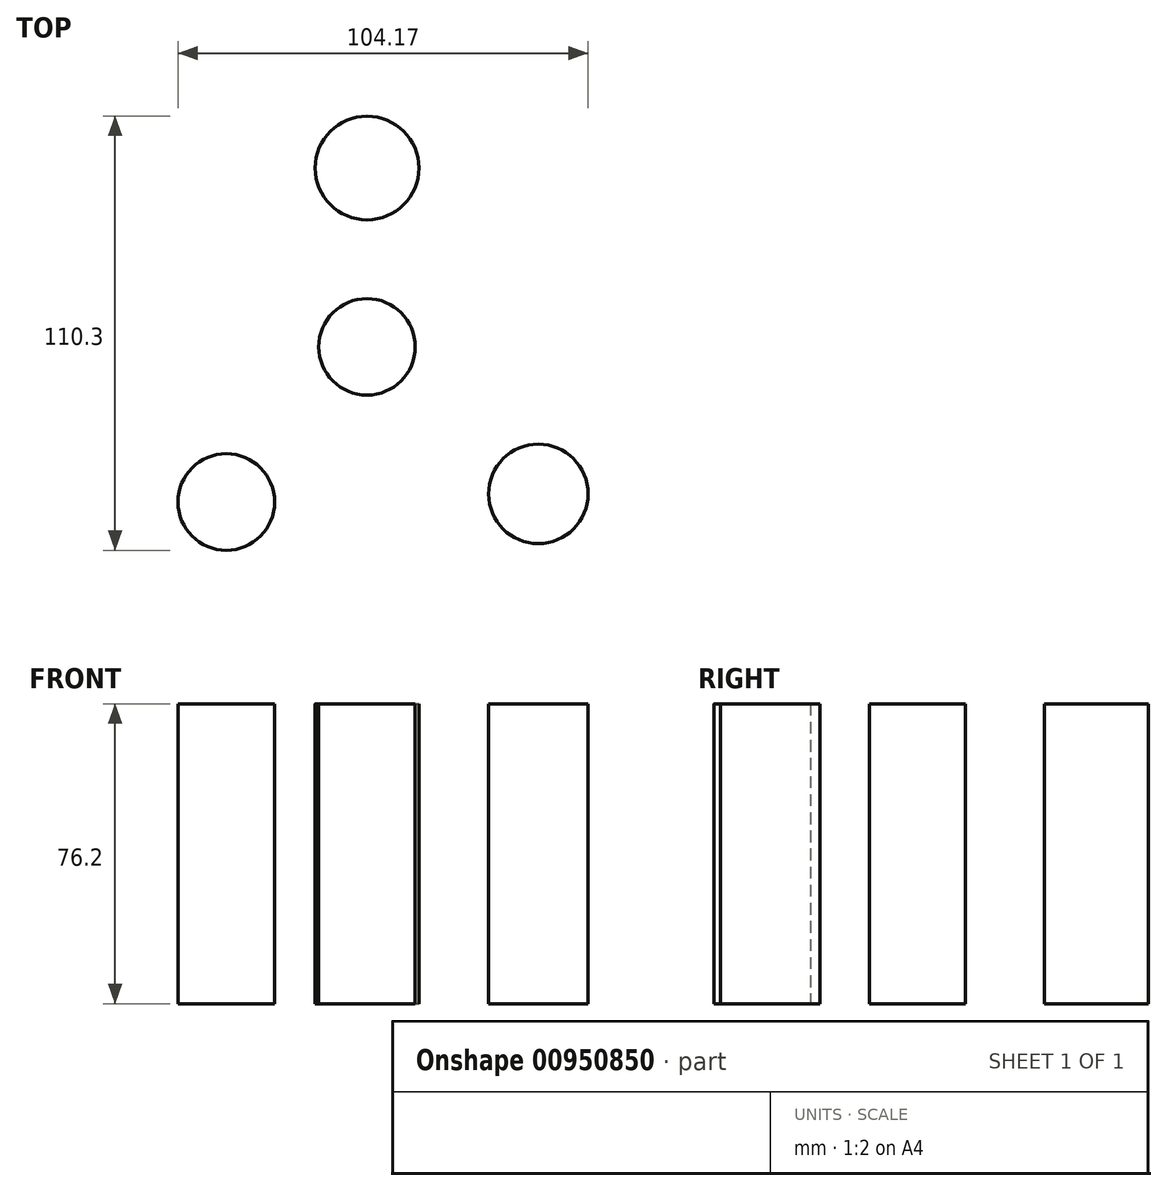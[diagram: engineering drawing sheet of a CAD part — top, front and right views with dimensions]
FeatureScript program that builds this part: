
annotation { "Feature Type Name" : "Feature", "Feature Type Description" : "" }
export const myFeature = defineFeature(function(context is Context, id is Id, definition is map)
    precondition{}
    {
        {
            var Q0;
            Q0=qCreatedBy(makeId("Top.planeOp"),FACE);
            var sketch = newSketch(context, id + "F0", { "sketchPlane" : qUnion([Q0])});
            skCircle(sketch, "E0", {"center": v(0, 0) * mm, "radius": 12.25 * mm});
            skCircle(sketch, "E1", {"center": v(0, 45.44) * mm, "radius": 13.18 * mm});
            skCircle(sketch, "E2", {"center": v(43.53, -37.36) * mm, "radius": 12.63 * mm});
            skCircle(sketch, "E3", {"center": v(-35.75, -39.42) * mm, "radius": 12.26 * mm});
            skArc(sketch, "E4", {"start": v(28.18, 45.43) * mm, "mid": v(-1.97, 68.83) * mm, "end": v(-30.98, 44.02) * mm});
            skSolve(sketch);
        }
        {
            var Q0;
            Q0=makeQuery(id+"F0.imprint","IMPRINT",FACE,{"disambiguationData":[TD([[makeQuery(id+"F0.imprint","IMPRINT",EDGE,{"derivedFrom":sQuery(id+"F0.wireOp",EDGE,"E1")}),1.0]])]});
            var Q1;
            Q1=makeQuery(id+"F0.imprint","IMPRINT",FACE,{"disambiguationData":[TD([[makeQuery(id+"F0.imprint","IMPRINT",EDGE,{"derivedFrom":sQuery(id+"F0.wireOp",EDGE,"E0")}),1.0]])]});
            var Q2;
            Q2=makeQuery(id+"F0.imprint","IMPRINT",FACE,{"disambiguationData":[TD([[makeQuery(id+"F0.imprint","IMPRINT",EDGE,{"derivedFrom":sQuery(id+"F0.wireOp",EDGE,"E2")}),1.0]])]});
            var Q3;
            Q3=makeQuery(id+"F0.imprint","IMPRINT",FACE,{"disambiguationData":[TD([[makeQuery(id+"F0.imprint","IMPRINT",EDGE,{"derivedFrom":sQuery(id+"F0.wireOp",EDGE,"E3")}),1.0]])]});
            extrude(context, id + "F1", {"entities" : qUnion([Q0, Q1, Q2, Q3]), "depth" : 76.2 * mm, "offsetDistance" : 25.4 * mm});
        }
    });
